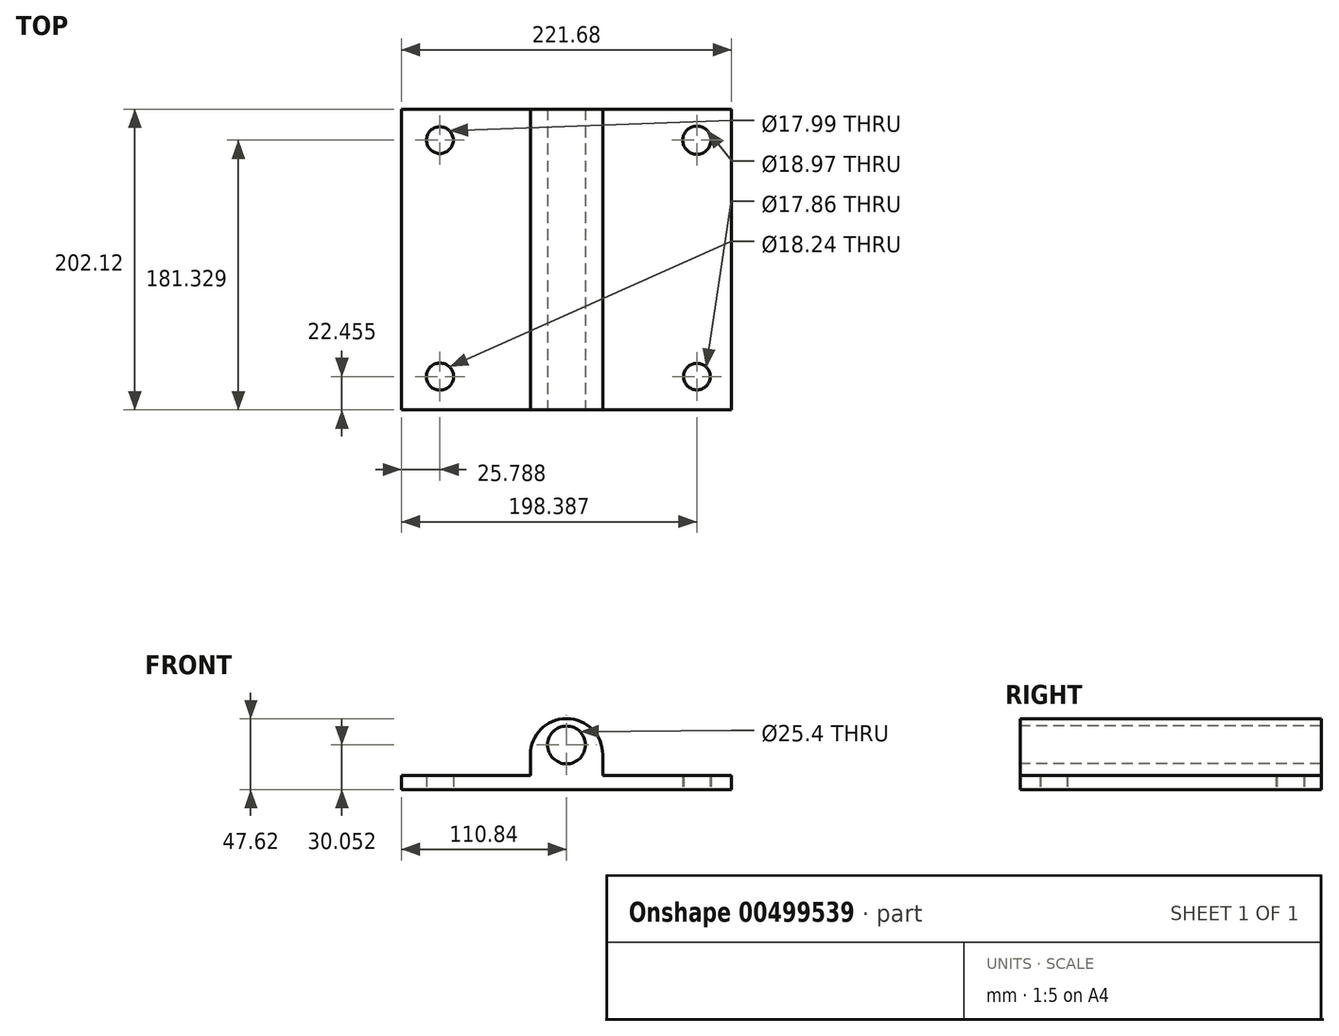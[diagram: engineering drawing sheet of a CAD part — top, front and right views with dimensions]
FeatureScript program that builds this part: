
annotation { "Feature Type Name" : "Feature", "Feature Type Description" : "" }
export const myFeature = defineFeature(function(context is Context, id is Id, definition is map)
    precondition{}
    {
        {
            var Q0;
            Q0=qCreatedBy(makeId("Top.planeOp"),FACE);
            var sketch = newSketch(context, id + "F0", { "sketchPlane" : qUnion([Q0])});
            skLineSegment(sketch, "E0.bottom", {"start": v(110.84, -101.06) * mm, "end": v(-110.84, -101.06) * mm});
            skLineSegment(sketch, "E0.top", {"start": v(110.84, 101.06) * mm, "end": v(-110.84, 101.06) * mm});
            skLineSegment(sketch, "E0.left", {"start": v(110.84, -101.06) * mm, "end": v(110.84, 101.06) * mm});
            skLineSegment(sketch, "E0.right", {"start": v(-110.84, -101.06) * mm, "end": v(-110.84, 101.06) * mm});
            skPoint(sketch, "E0.middle", {"position": v(0, 0) * mm});
            skPoint(sketch, "E1", {"position": v(-85.05, 80.27) * mm});
            skPoint(sketch, "E2", {"position": v(87.55, 80.27) * mm});
            skPoint(sketch, "E3", {"position": v(87.55, -78.6) * mm});
            skPoint(sketch, "E4", {"position": v(-85.05, -78.6) * mm});
            skCircle(sketch, "E5", {"center": v(-85.05, 80.27) * mm, "radius": 9 * mm});
            skCircle(sketch, "E6", {"center": v(87.55, 80.27) * mm, "radius": 9.48 * mm});
            skCircle(sketch, "E7", {"center": v(87.55, -78.6) * mm, "radius": 8.93 * mm});
            skCircle(sketch, "E8", {"center": v(-85.05, -78.6) * mm, "radius": 9.12 * mm});
            skSolve(sketch);
        }
        {
            var Q0;
            Q0=makeQuery(id+"F0.imprint","IMPRINT",FACE,{"disambiguationData":[TD([[makeQuery(id+"F0.imprint","IMPRINT",EDGE,{"derivedFrom":sQuery(id+"F0.wireOp",EDGE,"E0.bottom")}),-1.0]])]});
            extrude(context, id + "F1", {"entities" : qUnion([Q0]), "depth" : 9.52 * mm, "offsetDistance" : 25.4 * mm});
        }
        {
            var Q0;
            Q0=makeQuery(id+"F1.opExtrude","CAP_FACE",FACE,{"disambiguationData":[OSD([sQuery(id+"F0.wireOp",EDGE,"E0.bottom"),sQuery(id+"F0.wireOp",EDGE,"E0.top"),sQuery(id+"F0.wireOp",EDGE,"E0.left"),sQuery(id+"F0.wireOp",EDGE,"E0.right"),sQuery(id+"F0.wireOp",EDGE,"E5"),sQuery(id+"F0.wireOp",EDGE,"E6"),sQuery(id+"F0.wireOp",EDGE,"E7"),sQuery(id+"F0.wireOp",EDGE,"E8")])],"isStart":false});
            var sketch = newSketch(context, id + "F2", { "sketchPlane" : qUnion([Q0])});
            skLineSegment(sketch, "E9.bottom", {"start": v(24.34, -101.06) * mm, "end": v(-24.34, -101.06) * mm});
            skLineSegment(sketch, "E9.top", {"start": v(24.34, 101.06) * mm, "end": v(-24.34, 101.06) * mm});
            skLineSegment(sketch, "E9.left", {"start": v(24.34, -101.06) * mm, "end": v(24.34, 101.06) * mm});
            skLineSegment(sketch, "E9.right", {"start": v(-24.34, -101.06) * mm, "end": v(-24.34, 101.06) * mm});
            skPoint(sketch, "E9.middle", {"position": v(0, 0) * mm});
            skSolve(sketch);
        }
        {
            var Q0;
            Q0=makeQuery(id+"F2.imprint","IMPRINT",FACE,{"disambiguationData":[TD([[makeQuery(id+"F2.imprint","IMPRINT",EDGE,{"derivedFrom":sQuery(id+"F2.wireOp",EDGE,"E9.bottom")}),-1.0]])]});
            extrude(context, id + "F3", {"entities" : qUnion([Q0]), "operationType" : NewBodyOperationType.ADD, "depth" : 38.1 * mm, "offsetDistance" : 25.4 * mm});
        }
        {
            var Q0;
            Q0=makeQuery(id+"F3.boolean.opBoolean","MERGE",FACE,{"derivedFrom":[makeQuery(id+"F1.opExtrude","SWEPT_FACE",FACE,{"disambiguationData":[OSD([sQuery(id+"F0.wireOp",EDGE,"E0.bottom")])]}),makeQuery(id+"F3.opExtrude","SWEPT_FACE",FACE,{"disambiguationData":[OSD([sQuery(id+"F2.wireOp",EDGE,"E9.bottom")])]})]});
            var sketch = newSketch(context, id + "F4", { "sketchPlane" : qUnion([Q0])});
            skPoint(sketch, "E10", {"position": v(0, 30.05) * mm});
            skSolve(sketch);
        }
        {
            var Q0;
            Q0=sQuery(id+"F4.wireOp",VERTEX,"E10");
            var Q1;
            Q1=makeQuery(id+"F1.opExtrude","SWEPT_BODY",BODY,{"disambiguationData":[OSD([sQuery(id+"F0.wireOp",EDGE,"E0.bottom"),sQuery(id+"F0.wireOp",EDGE,"E0.top"),sQuery(id+"F0.wireOp",EDGE,"E0.left"),sQuery(id+"F0.wireOp",EDGE,"E0.right"),sQuery(id+"F0.wireOp",EDGE,"E5"),sQuery(id+"F0.wireOp",EDGE,"E6"),sQuery(id+"F0.wireOp",EDGE,"E7"),sQuery(id+"F0.wireOp",EDGE,"E8")])]});
            hole(context, id + "F5", {"style" : HoleStyle.SIMPLE, "endStyle" : HoleEndStyle.THROUGH, "holeDiameter" : 25.4 * mm, "isTappedThrough" : true, "tappedDepth" : 12.7 * mm, "tapClearance" : 3, "locations" : qUnion([Q0]), "scope" : qUnion([Q1])});
        }
        {
            var Q0;
            Q0=makeQuery(id+"F3.opExtrude","CAP_EDGE",EDGE,{"disambiguationData":[OSD([sQuery(id+"F2.wireOp",EDGE,"E9.right")])],"isStart":false});
            var Q1;
            Q1=makeQuery(id+"F3.opExtrude","CAP_EDGE",EDGE,{"disambiguationData":[OSD([sQuery(id+"F2.wireOp",EDGE,"E9.left")])],"isStart":false});
            fillet(context, id + "F6", {"entities" : qUnion([Q0, Q1]), "radius" : 24.13 * mm, "tangentPropagation" : true, "allowEdgeOverflow" : false});
        }
    });
